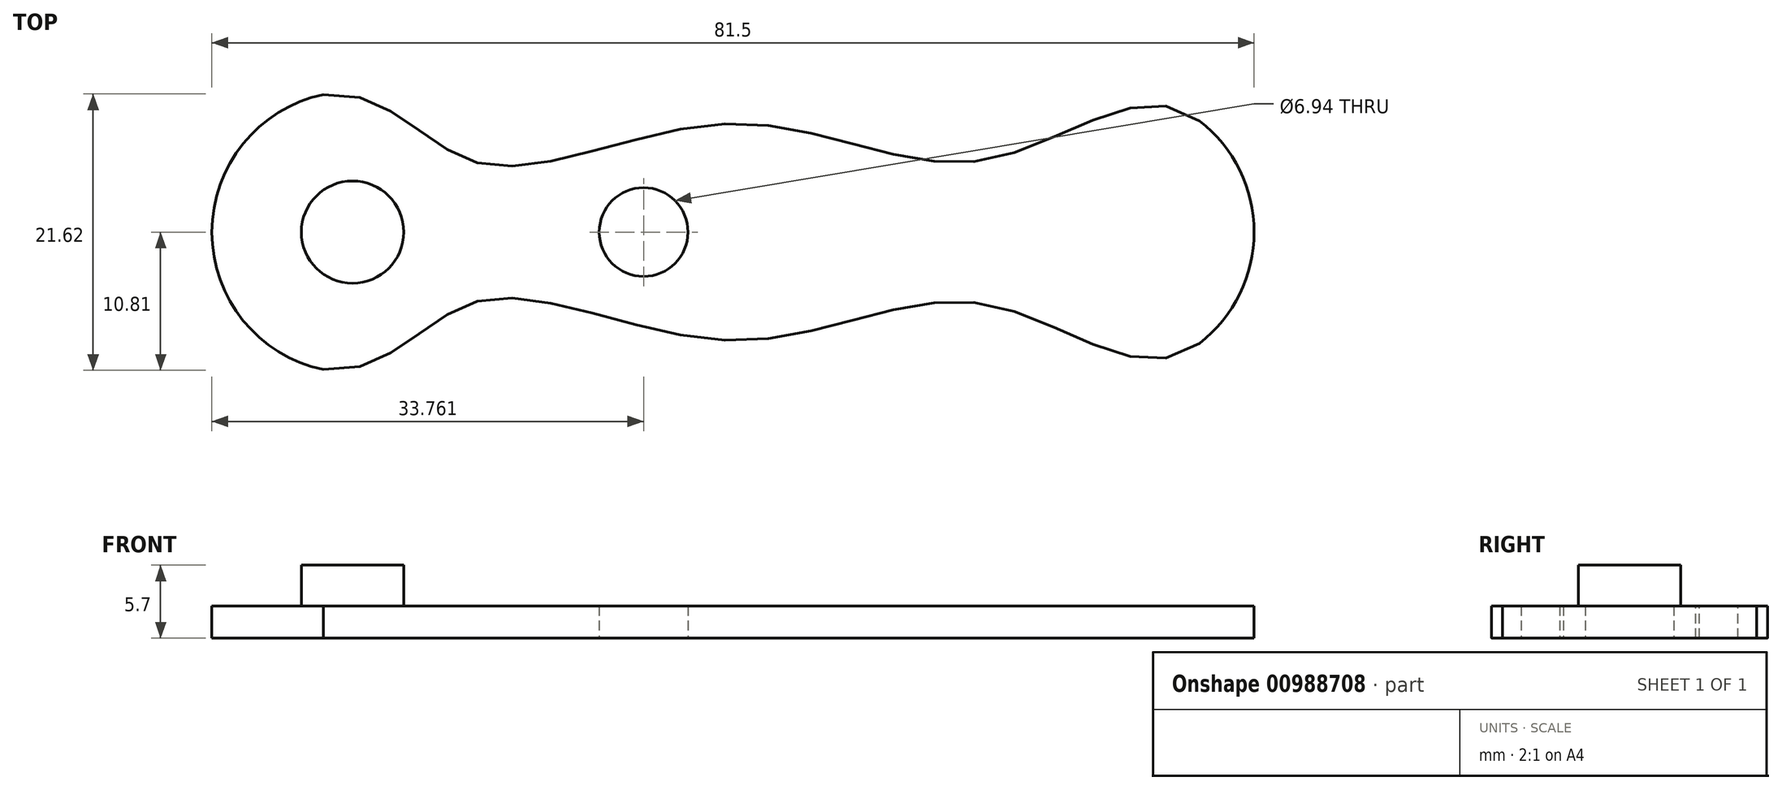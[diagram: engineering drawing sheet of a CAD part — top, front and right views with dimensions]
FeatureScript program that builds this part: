
annotation { "Feature Type Name" : "Feature", "Feature Type Description" : "" }
export const myFeature = defineFeature(function(context is Context, id is Id, definition is map)
    precondition{}
    {
        {
            var Q0;
            Q0=qCreatedBy(makeId("Top.planeOp"),FACE);
            var sketch = newSketch(context, id + "F0", { "sketchPlane" : qUnion([Q0])});
            skArc(sketch, "E0", {"start": v(-32.04, 10.76) * mm, "mid": v(-40.75, 0) * mm, "end": v(-32.04, -10.76) * mm});
            skLineSegment(sketch, "E1", {"start": v(0, 11.45) * mm, "end": v(0, -15.05) * mm, "construction": true});
            skArc(sketch, "E2", {"start": v(36.48, -8.7) * mm, "mid": v(40.75, 0) * mm, "end": v(36.48, 8.7) * mm});
            skFitSpline(sketch, "E3", {"points": [v(-32.04, -10.76) * mm, v(-20, -5.43) * mm, v(0, -8.49) * mm, v(20, -5.68) * mm, v(36.48, -8.7) * mm], "startDerivative": vector(72.29, -8.08) * mm, "endDerivative": vector(57.83, 44.77) * mm});
            skFitSpline(sketch, "E4.MirrorCS", {"points": [v(-32.04, 10.76) * mm, v(-20, 5.43) * mm, v(0, 8.49) * mm, v(20, 5.68) * mm, v(36.48, 8.7) * mm], "startDerivative": vector(72.29, 8.08) * mm, "endDerivative": vector(57.83, -44.77) * mm});
            skLineSegment(sketch, "E5", {"start": v(-20, -6.01) * mm, "end": v(20, -6.01) * mm, "construction": true});
            skFitSpline(sketch, "E6.0", {"points": [v(-31.27, 7.18) * mm, v(-30.75, 7.24) * mm, v(-30.07, 7.2) * mm, v(-29.22, 7) * mm, v(-28.37, 6.68) * mm, v(-27.26, 6.07) * mm, v(-25.81, 5.04) * mm, v(-24.47, 4.06) * mm, v(-23.27, 3.28) * mm, v(-22.3, 2.72) * mm, v(-21.4, 2.32) * mm, v(-20.62, 2.05) * mm, v(-20.01, 1.87) * mm, v(-19.4, 1.74) * mm, v(-18.57, 1.62) * mm, v(-17.54, 1.55) * mm, v(-16.3, 1.58) * mm, v(-14.67, 1.74) * mm, v(-12.63, 2.11) * mm, v(-10.18, 2.72) * mm, v(-7.73, 3.4) * mm, v(-5.3, 4.03) * mm, v(-3.33, 4.47) * mm, v(-1.8, 4.72) * mm, v(-0.67, 4.84) * mm, v(0.23, 4.9) * mm, v(0.93, 4.9) * mm, v(2, 4.86) * mm, v(3.62, 4.7) * mm, v(5.82, 4.26) * mm, v(8.09, 3.68) * mm, v(10.4, 3.06) * mm, v(12.8, 2.46) * mm, v(15.27, 2) * mm, v(17.41, 1.83) * mm, v(19.18, 1.88) * mm, v(20.3, 2) * mm, v(21.2, 2.17) * mm, v(22.09, 2.37) * mm, v(23.16, 2.69) * mm, v(24.4, 3.13) * mm, v(26, 3.78) * mm, v(27.87, 4.63) * mm, v(29.95, 5.53) * mm, v(31.48, 6.05) * mm, v(32.55, 6.28) * mm, v(33.25, 6.34) * mm, v(33.86, 6.32) * mm, v(34.4, 6.2) * mm, v(34.9, 6) * mm, v(35.26, 5.77) * mm, v(35.45, 5.62) * mm]});
            skLineSegment(sketch, "E7", {"start": v(-18, 0) * mm, "end": v(19.6, 0) * mm, "construction": true});
            skFitSpline(sketch, "E8.0", {"points": [v(-31.13, -7.22) * mm, v(-31.04, -7.23) * mm, v(-30.86, -7.25) * mm, v(-30.66, -7.25) * mm, v(-30.5, -7.24) * mm, v(-30.35, -7.23) * mm, v(-30.17, -7.2) * mm, v(-29.96, -7.16) * mm, v(-29.74, -7.1) * mm, v(-29.51, -7.02) * mm, v(-29.19, -6.89) * mm, v(-28.84, -6.72) * mm, v(-28.46, -6.5) * mm, v(-28.15, -6.31) * mm, v(-27.83, -6.1) * mm, v(-27.5, -5.88) * mm, v(-27.15, -5.63) * mm, v(-26.78, -5.37) * mm, v(-26.4, -5.08) * mm, v(-25.99, -4.79) * mm, v(-25.56, -4.49) * mm, v(-25.12, -4.18) * mm, v(-24.72, -3.92) * mm, v(-24.4, -3.7) * mm, v(-24.14, -3.55) * mm, v(-23.88, -3.4) * mm, v(-23.52, -3.2) * mm, v(-23.06, -2.94) * mm, v(-22.45, -2.66) * mm, v(-21.93, -2.44) * mm, v(-21.49, -2.27) * mm, v(-21.2, -2.18) * mm, v(-20.97, -2.1) * mm, v(-20.74, -2.04) * mm, v(-20.5, -1.97) * mm, v(-20.26, -1.92) * mm, v(-20.02, -1.87) * mm, v(-19.6, -1.78) * mm, v(-19, -1.7) * mm, v(-18.3, -1.63) * mm, v(-17.61, -1.6) * mm, v(-16.92, -1.6) * mm, v(-16.02, -1.64) * mm, v(-14.91, -1.75) * mm, v(-13.6, -1.95) * mm, v(-12.32, -2.2) * mm, v(-11.06, -2.5) * mm, v(-9.8, -2.82) * mm, v(-8.57, -3.15) * mm, v(-6.94, -3.6) * mm, v(-4.95, -4.12) * mm, v(-3.05, -4.53) * mm, v(-1.6, -4.77) * mm, v(-0.75, -4.86) * mm, v(-0.16, -4.9) * mm, v(0.16, -4.92) * mm, v(0.48, -4.93) * mm, v(0.88, -4.93) * mm, v(1.51, -4.91) * mm, v(2.33, -4.85) * mm, v(3.67, -4.68) * mm, v(5.42, -4.33) * mm, v(7.63, -3.78) * mm, v(9.56, -3.25) * mm, v(11.18, -2.84) * mm, v(12.21, -2.6) * mm, v(13.07, -2.42) * mm, v(13.92, -2.26) * mm, v(15.02, -2.08) * mm, v(16.4, -1.94) * mm, v(17.8, -1.88) * mm, v(19, -1.91) * mm, v(20, -2) * mm, v(20.73, -2.1) * mm, v(21.5, -2.24) * mm, v(22.22, -2.4) * mm, v(22.93, -2.6) * mm, v(23.85, -2.88) * mm, v(24.95, -3.28) * mm, v(26.2, -3.78) * mm, v(27.17, -4.2) * mm, v(27.92, -4.54) * mm, v(28.47, -4.79) * mm, v(29, -5.02) * mm, v(29.5, -5.24) * mm, v(30, -5.45) * mm, v(30.47, -5.64) * mm, v(30.92, -5.8) * mm, v(31.34, -5.96) * mm, v(31.73, -6.08) * mm, v(32.1, -6.18) * mm, v(32.45, -6.26) * mm, v(32.75, -6.32) * mm, v(33.02, -6.35) * mm, v(33.25, -6.37) * mm, v(33.45, -6.37) * mm, v(33.58, -6.35) * mm, v(33.68, -6.34) * mm, v(33.75, -6.33) * mm, v(33.82, -6.31) * mm, v(33.87, -6.3) * mm, v(33.93, -6.28) * mm, v(34, -6.25) * mm, v(34.06, -6.22) * mm, v(34.12, -6.2) * mm, v(34.18, -6.16) * mm, v(34.28, -6.1) * mm, v(34.36, -6.04) * mm, v(34.42, -6) * mm]});
            skCircle(sketch, "E9", {"center": v(-6.99, 0) * mm, "radius": 3.47 * mm});
            skPoint(sketch, "E9.first.point", {"position": v(-7.7, 3.4) * mm});
            skPoint(sketch, "E9.second.point", {"position": v(-7.55, -3.43) * mm});
            skPoint(sketch, "E9.third.point", {"position": v(-3.57, -0.6) * mm});
            skSolve(sketch);
        }
        {
            var Q0;
            Q0 = qSketchRegion(id + "F0", true);
            extrude(context, id + "F1", {"entities" : qUnion([Q0]), "depth" : 2.5 * mm, "offsetDistance" : 25 * mm});
        }
        {
            var Q0;
            Q0=makeQuery(id+"F1.opExtrude","CAP_FACE",FACE,{"disambiguationData":[OSD([sQuery(id+"F0.wireOp",EDGE,"E0"),sQuery(id+"F0.wireOp",EDGE,"E2"),sQuery(id+"F0.wireOp",EDGE,"E3"),sQuery(id+"F0.wireOp",EDGE,"E4.MirrorCS")])],"isStart":false});
            var sketch = newSketch(context, id + "F2", { "sketchPlane" : qUnion([Q0])});
            skCircle(sketch, "E10", {"center": v(-29.75, 0) * mm, "radius": 4 * mm});
            skCircle(sketch, "E11", {"center": v(29.75, 0) * mm, "radius": 4 * mm});
            skSolve(sketch);
        }
        {
            var Q0;
            Q0=makeQuery(id+"F2.imprint","IMPRINT",FACE,{"disambiguationData":[TD([[makeQuery(id+"F2.imprint","IMPRINT",EDGE,{"derivedFrom":sQuery(id+"F2.wireOp",EDGE,"E10")}),1.0]])]});
            var Q1;
            Q1=sQuery(id+"F2.wireOp",EDGE,"E10");
            extrude(context, id + "F3", {"entities" : qUnion([Q0]), "operationType" : NewBodyOperationType.ADD, "surfaceEntities" : qUnion([Q1]), "depth" : 3.2 * mm, "offsetDistance" : 25 * mm});
        }
    });
